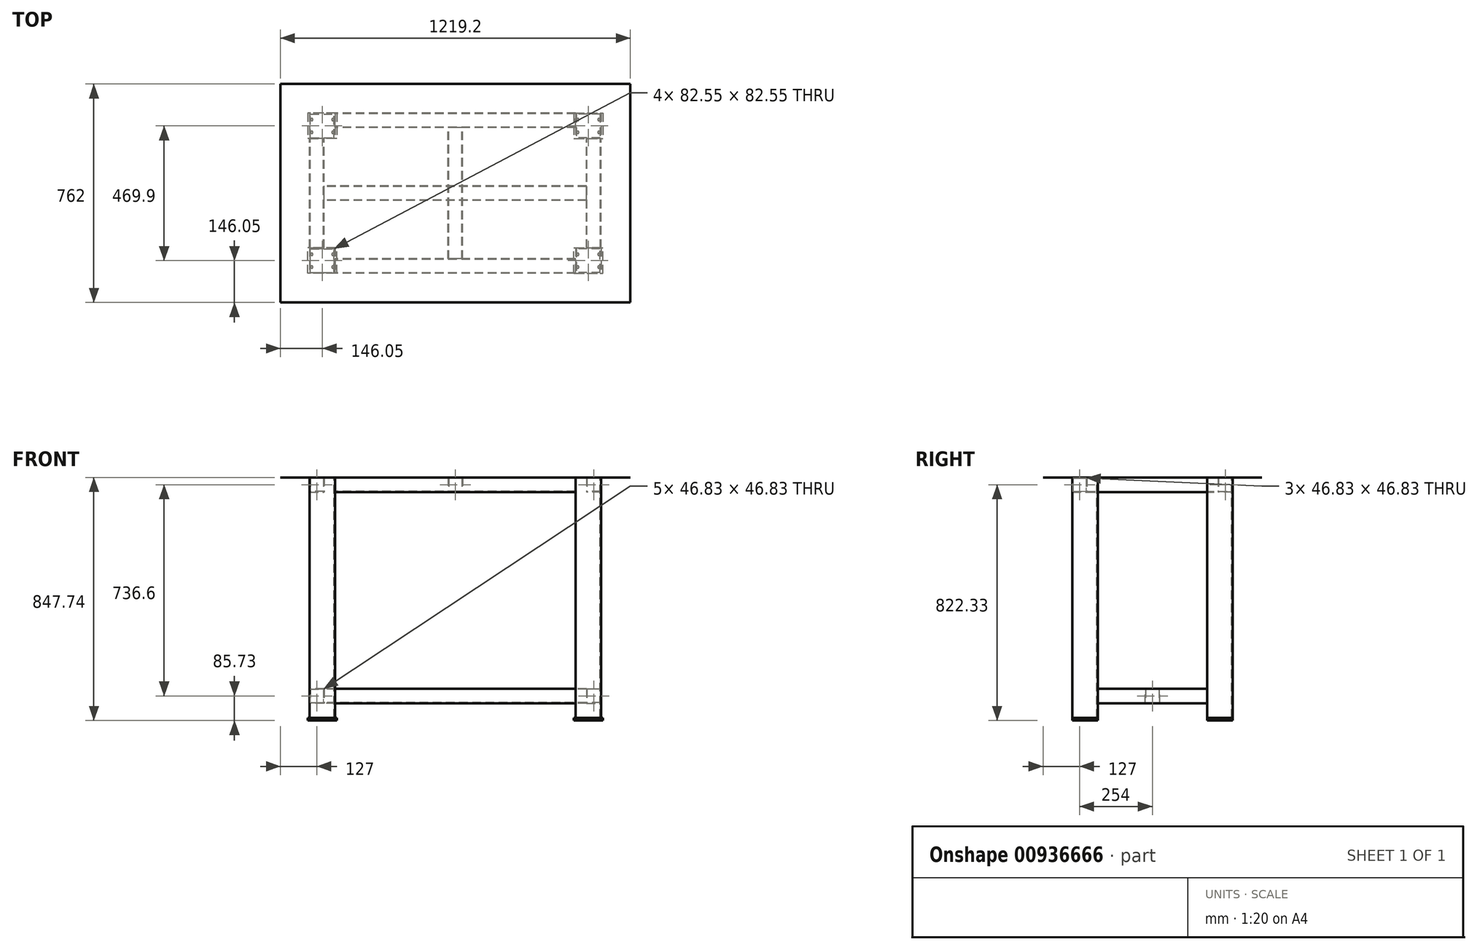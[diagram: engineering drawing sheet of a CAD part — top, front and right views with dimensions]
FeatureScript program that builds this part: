
annotation { "Feature Type Name" : "Feature", "Feature Type Description" : "" }
export const myFeature = defineFeature(function(context is Context, id is Id, definition is map)
    precondition{}
    {
        {
            var Q0;
            Q0=qCreatedBy(makeId("Top.planeOp"),FACE);
            var sketch = newSketch(context, id + "F0", { "sketchPlane" : qUnion([Q0])});
            skLineSegment(sketch, "E0.bottom", {"start": v(-419.1, 279.4) * mm, "end": v(-508, 279.4) * mm});
            skLineSegment(sketch, "E0.top", {"start": v(-419.1, 190.5) * mm, "end": v(-508, 190.5) * mm});
            skLineSegment(sketch, "E0.left", {"start": v(-419.1, 279.4) * mm, "end": v(-419.1, 190.5) * mm});
            skLineSegment(sketch, "E0.right", {"start": v(-508, 279.4) * mm, "end": v(-508, 190.5) * mm});
            skPoint(sketch, "E0.middle", {"position": v(-463.55, 234.95) * mm});
            skLineSegment(sketch, "E1.bottom", {"start": v(-419.1, -190.5) * mm, "end": v(-508, -190.5) * mm});
            skLineSegment(sketch, "E1.top", {"start": v(-419.1, -279.4) * mm, "end": v(-508, -279.4) * mm});
            skLineSegment(sketch, "E1.left", {"start": v(-419.1, -190.5) * mm, "end": v(-419.1, -279.4) * mm});
            skLineSegment(sketch, "E1.right", {"start": v(-508, -190.5) * mm, "end": v(-508, -279.4) * mm});
            skPoint(sketch, "E1.middle", {"position": v(-463.55, -234.95) * mm});
            skPoint(sketch, "E2.MirrorP", {"position": v(463.55, -234.95) * mm});
            skLineSegment(sketch, "E3.MirrorCS", {"start": v(419.1, 190.5) * mm, "end": v(508, 190.5) * mm});
            skLineSegment(sketch, "E4.MirrorCS", {"start": v(419.1, -190.5) * mm, "end": v(419.1, -279.4) * mm});
            skLineSegment(sketch, "E5.MirrorCS", {"start": v(419.1, 279.4) * mm, "end": v(419.1, 190.5) * mm});
            skLineSegment(sketch, "E6.MirrorCS", {"start": v(419.1, 279.4) * mm, "end": v(508, 279.4) * mm});
            skPoint(sketch, "E7.MirrorP", {"position": v(463.55, 234.95) * mm});
            skLineSegment(sketch, "E8.MirrorCS", {"start": v(419.1, -190.5) * mm, "end": v(508, -190.5) * mm});
            skLineSegment(sketch, "E9.MirrorCS", {"start": v(508, 279.4) * mm, "end": v(508, 190.5) * mm});
            skLineSegment(sketch, "E10.MirrorCS", {"start": v(419.1, -279.4) * mm, "end": v(508, -279.4) * mm});
            skLineSegment(sketch, "E11.MirrorCS", {"start": v(508, -190.5) * mm, "end": v(508, -279.4) * mm});
            skLineSegment(sketch, "E12.bottom", {"start": v(-504.83, 193.67) * mm, "end": v(-422.28, 193.67) * mm});
            skLineSegment(sketch, "E12.top", {"start": v(-504.83, 276.23) * mm, "end": v(-422.28, 276.23) * mm});
            skLineSegment(sketch, "E12.left", {"start": v(-504.83, 193.67) * mm, "end": v(-504.83, 276.23) * mm});
            skLineSegment(sketch, "E12.right", {"start": v(-422.28, 193.67) * mm, "end": v(-422.28, 276.23) * mm});
            skLineSegment(sketch, "E13.bottom", {"start": v(-504.83, -276.23) * mm, "end": v(-422.27, -276.23) * mm});
            skLineSegment(sketch, "E13.top", {"start": v(-504.83, -193.68) * mm, "end": v(-422.27, -193.68) * mm});
            skLineSegment(sketch, "E13.left", {"start": v(-504.83, -276.23) * mm, "end": v(-504.83, -193.68) * mm});
            skLineSegment(sketch, "E13.right", {"start": v(-422.27, -276.23) * mm, "end": v(-422.27, -193.68) * mm});
            skLineSegment(sketch, "E14.MirrorCS", {"start": v(-419.1, 190.5) * mm, "end": v(-419.1, 279.4) * mm});
            skLineSegment(sketch, "E15.MirrorCS", {"start": v(-504.83, 193.68) * mm, "end": v(-422.27, 193.68) * mm});
            skLineSegment(sketch, "E16.MirrorCS", {"start": v(-504.83, 276.23) * mm, "end": v(-422.27, 276.23) * mm});
            skLineSegment(sketch, "E17.MirrorCS", {"start": v(-504.83, 276.23) * mm, "end": v(-504.83, 193.68) * mm});
            skLineSegment(sketch, "E18.MirrorCS", {"start": v(-508, 190.5) * mm, "end": v(-508, 279.4) * mm});
            skLineSegment(sketch, "E19.MirrorCS", {"start": v(-422.27, 276.23) * mm, "end": v(-422.27, 193.68) * mm});
            skLineSegment(sketch, "E20.MirrorCS", {"start": v(-419.1, -279.4) * mm, "end": v(-419.1, -190.5) * mm});
            skLineSegment(sketch, "E21.MirrorCS", {"start": v(-422.28, -193.67) * mm, "end": v(-422.28, -276.23) * mm});
            skLineSegment(sketch, "E22.MirrorCS", {"start": v(504.83, 193.67) * mm, "end": v(422.28, 193.67) * mm});
            skLineSegment(sketch, "E23.MirrorCS", {"start": v(508, 190.5) * mm, "end": v(508, 279.4) * mm});
            skLineSegment(sketch, "E24.MirrorCS", {"start": v(422.28, -193.67) * mm, "end": v(422.28, -276.23) * mm});
            skLineSegment(sketch, "E25.MirrorCS", {"start": v(419.1, -279.4) * mm, "end": v(419.1, -190.5) * mm});
            skLineSegment(sketch, "E26.MirrorCS", {"start": v(504.83, 193.68) * mm, "end": v(422.27, 193.68) * mm});
            skLineSegment(sketch, "E27.MirrorCS", {"start": v(419.1, 190.5) * mm, "end": v(419.1, 279.4) * mm});
            skLineSegment(sketch, "E28.MirrorCS", {"start": v(504.83, -193.68) * mm, "end": v(422.27, -193.68) * mm});
            skLineSegment(sketch, "E29.MirrorCS", {"start": v(504.83, 276.23) * mm, "end": v(422.27, 276.23) * mm});
            skLineSegment(sketch, "E30.MirrorCS", {"start": v(422.27, -276.23) * mm, "end": v(422.27, -193.68) * mm});
            skLineSegment(sketch, "E31.MirrorCS", {"start": v(422.27, 276.23) * mm, "end": v(422.27, 193.68) * mm});
            skLineSegment(sketch, "E32.MirrorCS", {"start": v(504.83, 276.23) * mm, "end": v(504.83, 193.68) * mm});
            skLineSegment(sketch, "E33.MirrorCS", {"start": v(504.83, -276.23) * mm, "end": v(422.27, -276.23) * mm});
            skLineSegment(sketch, "E34.MirrorCS", {"start": v(422.28, 193.67) * mm, "end": v(422.28, 276.23) * mm});
            skLineSegment(sketch, "E35.MirrorCS", {"start": v(504.83, 193.67) * mm, "end": v(504.83, 276.23) * mm});
            skLineSegment(sketch, "E36.MirrorCS", {"start": v(504.83, 276.23) * mm, "end": v(422.28, 276.23) * mm});
            skLineSegment(sketch, "E37.MirrorCS", {"start": v(504.83, -276.23) * mm, "end": v(504.83, -193.68) * mm});
            skSolve(sketch);
        }
        {
            var Q0;
            Q0=makeQuery(id+"F0.imprint","IMPRINT",FACE,{"disambiguationData":[TD([[makeQuery(id+"F0.imprint","IMPRINT",EDGE,{"derivedFrom":sQuery(id+"F0.wireOp",EDGE,"E28.MirrorCS")}),-1.0]])]});
            var Q1;
            Q1=makeQuery(id+"F0.imprint","IMPRINT",FACE,{"disambiguationData":[TD([[makeQuery(id+"F0.imprint","IMPRINT",EDGE,{"derivedFrom":sQuery(id+"F0.wireOp",EDGE,"E26.MirrorCS")}),1.0]])]});
            var Q2;
            Q2=makeQuery(id+"F0.imprint","IMPRINT",FACE,{"disambiguationData":[TD([[makeQuery(id+"F0.imprint","IMPRINT",EDGE,{"derivedFrom":sQuery(id+"F0.wireOp",EDGE,"E1.top")}),-1.0]])]});
            var Q3;
            Q3=makeQuery(id+"F0.imprint","IMPRINT",FACE,{"disambiguationData":[TD([[makeQuery(id+"F0.imprint","IMPRINT",EDGE,{"derivedFrom":sQuery(id+"F0.wireOp",EDGE,"E15.MirrorCS")}),-1.0]])]});
            extrude(context, id + "F1", {"entities" : qUnion([Q0, Q1, Q2, Q3]), "oppositeDirection" : true, "depth" : 838.2 * mm, "offsetDistance" : 25.4 * mm});
        }
        {
            var Q0;
            Q0=qCreatedBy(makeId("Right.planeOp"),FACE);
            var sketch = newSketch(context, id + "F2", { "sketchPlane" : qUnion([Q0])});
            skLineSegment(sketch, "E38.bottom", {"start": v(-279.4, 0) * mm, "end": v(-228.6, 0) * mm});
            skLineSegment(sketch, "E38.top", {"start": v(-279.4, -50.8) * mm, "end": v(-228.6, -50.8) * mm});
            skLineSegment(sketch, "E38.left", {"start": v(-279.4, 0) * mm, "end": v(-279.4, -50.8) * mm});
            skLineSegment(sketch, "E38.right", {"start": v(-228.6, 0) * mm, "end": v(-228.6, -50.8) * mm});
            skLineSegment(sketch, "E39.bottom", {"start": v(279.4, 0) * mm, "end": v(228.6, 0) * mm});
            skLineSegment(sketch, "E39.top", {"start": v(279.4, -50.8) * mm, "end": v(228.6, -50.8) * mm});
            skLineSegment(sketch, "E39.left", {"start": v(228.6, 0) * mm, "end": v(228.6, -50.8) * mm});
            skLineSegment(sketch, "E39.right", {"start": v(279.4, 0) * mm, "end": v(279.4, -50.8) * mm});
            skLineSegment(sketch, "E40.bottom", {"start": v(230.58, -1.98) * mm, "end": v(277.42, -1.98) * mm});
            skLineSegment(sketch, "E40.top", {"start": v(230.58, -48.82) * mm, "end": v(277.42, -48.82) * mm});
            skLineSegment(sketch, "E40.left", {"start": v(230.58, -1.98) * mm, "end": v(230.58, -48.82) * mm});
            skLineSegment(sketch, "E40.right", {"start": v(277.42, -1.98) * mm, "end": v(277.42, -48.82) * mm});
            skPoint(sketch, "E40.middle", {"position": v(254, -25.4) * mm});
            skPoint(sketch, "E40.middle.positionSnap0", {"position": v(254, -50.8) * mm});
            skPoint(sketch, "E40.centerSnap0", {"position": v(254, -50.8) * mm});
            skLineSegment(sketch, "E41.bottom", {"start": v(-277.42, -1.98) * mm, "end": v(-230.58, -1.98) * mm});
            skLineSegment(sketch, "E41.top", {"start": v(-277.42, -48.82) * mm, "end": v(-230.58, -48.82) * mm});
            skLineSegment(sketch, "E41.left", {"start": v(-277.42, -1.98) * mm, "end": v(-277.42, -48.82) * mm});
            skLineSegment(sketch, "E41.right", {"start": v(-230.58, -1.98) * mm, "end": v(-230.58, -48.82) * mm});
            skPoint(sketch, "E41.middle", {"position": v(-254, -25.4) * mm});
            skPoint(sketch, "E41.middle.positionSnap0", {"position": v(-228.6, -25.4) * mm});
            skPoint(sketch, "E41.centerSnap0", {"position": v(-228.6, -25.4) * mm});
            skSolve(sketch);
        }
        {
            var Q0;
            Q0=qSketchRegion(id+"F2",true);
            extrude(context, id + "F3", {"entities" : qUnion([Q0]), "depth" : 419.1 * mm, "offsetDistance" : 25.4 * mm, "hasSecondDirection" : true, "secondDirectionOppositeDirection" : true, "secondDirectionDepth" : 419.1 * mm});
        }
        {
            var Q0;
            Q0=qCreatedBy(makeId("Front.planeOp"),FACE);
            var sketch = newSketch(context, id + "F4", { "sketchPlane" : qUnion([Q0])});
            skLineSegment(sketch, "E42.bottom", {"start": v(-508, 0) * mm, "end": v(-457.2, 0) * mm});
            skLineSegment(sketch, "E42.top", {"start": v(-508, -50.8) * mm, "end": v(-457.2, -50.8) * mm});
            skLineSegment(sketch, "E42.left", {"start": v(-508, 0) * mm, "end": v(-508, -50.8) * mm});
            skLineSegment(sketch, "E42.right", {"start": v(-457.2, 0) * mm, "end": v(-457.2, -50.8) * mm});
            skLineSegment(sketch, "E43.bottom", {"start": v(508, 0) * mm, "end": v(457.2, 0) * mm});
            skLineSegment(sketch, "E43.top", {"start": v(508, -50.8) * mm, "end": v(457.2, -50.8) * mm});
            skLineSegment(sketch, "E43.left", {"start": v(508, 0) * mm, "end": v(508, -50.8) * mm});
            skLineSegment(sketch, "E43.right", {"start": v(457.2, 0) * mm, "end": v(457.2, -50.8) * mm});
            skLineSegment(sketch, "E44.bottom", {"start": v(-457.2, -736.6) * mm, "end": v(-508, -736.6) * mm});
            skLineSegment(sketch, "E44.top", {"start": v(-457.2, -787.4) * mm, "end": v(-508, -787.4) * mm});
            skLineSegment(sketch, "E44.left", {"start": v(-457.2, -736.6) * mm, "end": v(-457.2, -787.4) * mm});
            skLineSegment(sketch, "E44.right", {"start": v(-508, -736.6) * mm, "end": v(-508, -787.4) * mm});
            skLineSegment(sketch, "E45.bottom", {"start": v(457.2, -736.6) * mm, "end": v(508, -736.6) * mm});
            skLineSegment(sketch, "E45.top", {"start": v(457.2, -787.4) * mm, "end": v(508, -787.4) * mm});
            skLineSegment(sketch, "E45.left", {"start": v(457.2, -736.6) * mm, "end": v(457.2, -787.4) * mm});
            skLineSegment(sketch, "E45.right", {"start": v(508, -736.6) * mm, "end": v(508, -787.4) * mm});
            skLineSegment(sketch, "E46.bottom", {"start": v(-459.18, -1.98) * mm, "end": v(-506.02, -1.98) * mm});
            skLineSegment(sketch, "E46.top", {"start": v(-459.18, -48.82) * mm, "end": v(-506.02, -48.82) * mm});
            skLineSegment(sketch, "E46.left", {"start": v(-459.18, -1.98) * mm, "end": v(-459.18, -48.82) * mm});
            skLineSegment(sketch, "E46.right", {"start": v(-506.02, -1.98) * mm, "end": v(-506.02, -48.82) * mm});
            skPoint(sketch, "E46.middle", {"position": v(-482.6, -25.4) * mm});
            skPoint(sketch, "E46.middle.positionSnap0", {"position": v(-508, -25.4) * mm});
            skPoint(sketch, "E46.centerSnap0", {"position": v(-508, -25.4) * mm});
            skLineSegment(sketch, "E47.bottom", {"start": v(-506.02, -738.58) * mm, "end": v(-459.18, -738.58) * mm});
            skLineSegment(sketch, "E47.top", {"start": v(-506.02, -785.42) * mm, "end": v(-459.18, -785.42) * mm});
            skLineSegment(sketch, "E47.left", {"start": v(-506.02, -738.58) * mm, "end": v(-506.02, -785.42) * mm});
            skLineSegment(sketch, "E47.right", {"start": v(-459.18, -738.58) * mm, "end": v(-459.18, -785.42) * mm});
            skPoint(sketch, "E47.middle", {"position": v(-482.6, -762) * mm});
            skPoint(sketch, "E47.middle.positionSnap0", {"position": v(-457.2, -762) * mm});
            skPoint(sketch, "E47.centerSnap0", {"position": v(-457.2, -762) * mm});
            skLineSegment(sketch, "E48.bottom", {"start": v(506.02, -738.58) * mm, "end": v(459.18, -738.58) * mm});
            skLineSegment(sketch, "E48.top", {"start": v(506.02, -785.42) * mm, "end": v(459.18, -785.42) * mm});
            skLineSegment(sketch, "E48.left", {"start": v(506.02, -738.58) * mm, "end": v(506.02, -785.42) * mm});
            skLineSegment(sketch, "E48.right", {"start": v(459.18, -738.58) * mm, "end": v(459.18, -785.42) * mm});
            skPoint(sketch, "E48.middle", {"position": v(482.6, -762) * mm});
            skPoint(sketch, "E48.middle.positionSnap0", {"position": v(457.2, -762) * mm});
            skPoint(sketch, "E48.centerSnap0", {"position": v(457.2, -762) * mm});
            skLineSegment(sketch, "E49.bottom", {"start": v(506.02, -1.98) * mm, "end": v(459.18, -1.98) * mm});
            skLineSegment(sketch, "E49.top", {"start": v(506.02, -48.82) * mm, "end": v(459.18, -48.82) * mm});
            skLineSegment(sketch, "E49.left", {"start": v(506.02, -1.98) * mm, "end": v(506.02, -48.82) * mm});
            skLineSegment(sketch, "E49.right", {"start": v(459.18, -1.98) * mm, "end": v(459.18, -48.82) * mm});
            skPoint(sketch, "E49.middle", {"position": v(482.6, -25.4) * mm});
            skSolve(sketch);
        }
        {
            var Q0;
            Q0=qSketchRegion(id+"F4",true);
            extrude(context, id + "F5", {"entities" : qUnion([Q0]), "depth" : 190.5 * mm, "offsetDistance" : 25.4 * mm, "hasSecondDirection" : true, "secondDirectionOppositeDirection" : true, "secondDirectionDepth" : 190.5 * mm});
        }
        {
            var Q0;
            Q0=qCreatedBy(makeId("Right.planeOp"),FACE);
            var sketch = newSketch(context, id + "F6", { "sketchPlane" : qUnion([Q0])});
            skLineSegment(sketch, "E50.bottom", {"start": v(-25.4, -787.4) * mm, "end": v(25.4, -787.4) * mm});
            skLineSegment(sketch, "E50.top", {"start": v(-25.4, -736.6) * mm, "end": v(25.4, -736.6) * mm});
            skLineSegment(sketch, "E50.left", {"start": v(-25.4, -787.4) * mm, "end": v(-25.4, -736.6) * mm});
            skLineSegment(sketch, "E50.right", {"start": v(25.4, -787.4) * mm, "end": v(25.4, -736.6) * mm});
            skLineSegment(sketch, "E51.bottom", {"start": v(-23.42, -738.58) * mm, "end": v(23.42, -738.58) * mm});
            skLineSegment(sketch, "E51.top", {"start": v(-23.42, -785.42) * mm, "end": v(23.42, -785.42) * mm});
            skLineSegment(sketch, "E51.left", {"start": v(-23.42, -738.58) * mm, "end": v(-23.42, -785.42) * mm});
            skLineSegment(sketch, "E51.right", {"start": v(23.42, -738.58) * mm, "end": v(23.42, -785.42) * mm});
            skPoint(sketch, "E51.middle", {"position": v(0, -762) * mm});
            skPoint(sketch, "E51.middle.positionSnap0", {"position": v(-25.4, -762) * mm});
            skPoint(sketch, "E51.centerSnap0", {"position": v(-25.4, -762) * mm});
            skSolve(sketch);
        }
        {
            var Q0;
            Q0=makeQuery(id+"F6.imprint","IMPRINT",FACE,{"disambiguationData":[TD([[makeQuery(id+"F6.imprint","IMPRINT",EDGE,{"derivedFrom":sQuery(id+"F6.wireOp",EDGE,"E50.bottom")}),1.0]])]});
            extrude(context, id + "F7", {"entities" : qUnion([Q0]), "depth" : 457.2 * mm, "offsetDistance" : 25.4 * mm, "hasSecondDirection" : true, "secondDirectionOppositeDirection" : true, "secondDirectionDepth" : 457.2 * mm});
        }
        {
            var Q0;
            Q0=qCreatedBy(makeId("Top.planeOp"),FACE);
            var sketch = newSketch(context, id + "F8", { "sketchPlane" : qUnion([Q0])});
            skLineSegment(sketch, "E52.bottom", {"start": v(609.6, -381) * mm, "end": v(-609.6, -381) * mm});
            skLineSegment(sketch, "E52.top", {"start": v(609.6, 381) * mm, "end": v(-609.6, 381) * mm});
            skLineSegment(sketch, "E52.left", {"start": v(609.6, -381) * mm, "end": v(609.6, 381) * mm});
            skLineSegment(sketch, "E52.right", {"start": v(-609.6, -381) * mm, "end": v(-609.6, 381) * mm});
            skPoint(sketch, "E52.middle", {"position": v(0, 0) * mm});
            skSolve(sketch);
        }
        {
            var Q0;
            Q0=qSketchRegion(id+"F8",true);
            extrude(context, id + "F9", {"entities" : qUnion([Q0]), "depth" : 3 / 203.2 * mm, "offsetDistance" : 25.4 * mm});
        }
        {
            var Q0;
            Q0=makeQuery(id+"F1.opExtrude","CAP_FACE",FACE,{"disambiguationData":[OSD([sQuery(id+"F0.wireOp",EDGE,"E1.top"),sQuery(id+"F0.wireOp",EDGE,"E1.right"),sQuery(id+"F0.wireOp",EDGE,"E1.bottom"),sQuery(id+"F0.wireOp",EDGE,"E13.bottom"),sQuery(id+"F0.wireOp",EDGE,"E13.top"),sQuery(id+"F0.wireOp",EDGE,"E13.left"),sQuery(id+"F0.wireOp",EDGE,"E20.MirrorCS"),sQuery(id+"F0.wireOp",EDGE,"E21.MirrorCS")])],"isStart":false});
            cPlane(context, id + "F10", {"entities" : qUnion([Q0]), "cplaneType" : CPlaneType.OFFSET, "offset" : 0 * mm, "width" : 152.4 * mm, "height" : 152.4 * mm});
        }
        {
            var Q0;
            Q0=qCreatedBy(id+"F10.planeOp",FACE);
            var sketch = newSketch(context, id + "F11", { "sketchPlane" : qUnion([Q0])});
            skLineSegment(sketch, "E53.bottom", {"start": v(-412.75, 279.4) * mm, "end": v(-514.35, 279.4) * mm});
            skLineSegment(sketch, "E53.top", {"start": v(-412.75, 190.5) * mm, "end": v(-514.35, 190.5) * mm});
            skLineSegment(sketch, "E53.left", {"start": v(-412.75, 279.4) * mm, "end": v(-412.75, 190.5) * mm});
            skLineSegment(sketch, "E53.right", {"start": v(-514.35, 279.4) * mm, "end": v(-514.35, 190.5) * mm});
            skPoint(sketch, "E53.middle", {"position": v(-463.55, 234.95) * mm});
            skSolve(sketch);
        }
        {
            var Q0;
            Q0=qSketchRegion(id+"F11",true);
            extrude(context, id + "F12", {"entities" : qUnion([Q0]), "depth" : 9.52 * mm, "offsetDistance" : 25.4 * mm});
        }
        {
            var Q0;
            Q0=makeQuery(id+"F12.opExtrude","CAP_FACE",FACE,{"disambiguationData":[OSD([sQuery(id+"F11.wireOp",EDGE,"E53.bottom"),sQuery(id+"F11.wireOp",EDGE,"E53.top"),sQuery(id+"F11.wireOp",EDGE,"E53.left"),sQuery(id+"F11.wireOp",EDGE,"E53.right")])],"isStart":false});
            cPlane(context, id + "F13", {"entities" : qUnion([Q0]), "cplaneType" : CPlaneType.OFFSET, "offset" : 0 * mm, "width" : 152.4 * mm, "height" : 152.4 * mm});
        }
        {
            var Q0;
            Q0=qCreatedBy(id+"F13.planeOp",FACE);
            var sketch = newSketch(context, id + "F14", { "sketchPlane" : qUnion([Q0])});
            skCircle(sketch, "E54", {"center": v(-427.04, 257.18) * mm, "radius": 4.76 * mm});
            skCircle(sketch, "E55", {"center": v(-427.04, 212.73) * mm, "radius": 4.76 * mm});
            skCircle(sketch, "E56", {"center": v(-500.06, 212.73) * mm, "radius": 4.76 * mm});
            skCircle(sketch, "E57", {"center": v(-500.06, 257.18) * mm, "radius": 4.76 * mm});
            skSolve(sketch);
        }
        {
            var Q0;
            Q0=sQuery(id+"F14.wireOp",VERTEX,"E57.center");
            var Q1;
            Q1=sQuery(id+"F14.wireOp",VERTEX,"E56.center");
            var Q2;
            Q2=sQuery(id+"F14.wireOp",VERTEX,"E55.center");
            var Q3;
            Q3=sQuery(id+"F14.wireOp",VERTEX,"E54.center");
            var Q4;
            Q4=makeQuery(id+"F1.opExtrude","SWEPT_BODY",BODY,{"disambiguationData":[OSD([sQuery(id+"F0.wireOp",EDGE,"E1.top"),sQuery(id+"F0.wireOp",EDGE,"E1.right"),sQuery(id+"F0.wireOp",EDGE,"E1.bottom"),sQuery(id+"F0.wireOp",EDGE,"E13.bottom"),sQuery(id+"F0.wireOp",EDGE,"E13.top"),sQuery(id+"F0.wireOp",EDGE,"E13.left"),sQuery(id+"F0.wireOp",EDGE,"E20.MirrorCS"),sQuery(id+"F0.wireOp",EDGE,"E21.MirrorCS")])]});
            var Q5;
            Q5=makeQuery(id+"F9.opExtrude","SWEPT_BODY",BODY,{"disambiguationData":[OSD([sQuery(id+"F8.wireOp",EDGE,"E52.bottom"),sQuery(id+"F8.wireOp",EDGE,"E52.top"),sQuery(id+"F8.wireOp",EDGE,"E52.left"),sQuery(id+"F8.wireOp",EDGE,"E52.right")])]});
            var Q6;
            Q6=makeQuery(id+"F12.opExtrude","SWEPT_BODY",BODY,{"disambiguationData":[OSD([sQuery(id+"F11.wireOp",EDGE,"E53.bottom"),sQuery(id+"F11.wireOp",EDGE,"E53.top"),sQuery(id+"F11.wireOp",EDGE,"E53.left"),sQuery(id+"F11.wireOp",EDGE,"E53.right")])]});
            hole(context, id + "F15", {"style" : HoleStyle.SIMPLE, "endStyle" : HoleEndStyle.BLIND, "standardTappedOrClearance" : lookupTablePath({ "standard" : "ANSI", "engagement" : "75%", "pitch" : "16 tpi", "size" : "3/8", "type" : "Tapped" }), "standardBlindInLast" : lookupTablePath({ "standard" : "ANSI", "engagement" : "75%", "pitch" : "16 tpi", "size" : "3/8", "type" : "Tapped" }), "holeDiameter" : 7.94 * mm, "majorDiameter" : 9.52 * mm, "showTappedDepth" : true, "holeDepth" : 9.52 * mm, "isTappedThrough" : true, "tappedDepth" : 4.76 * mm, "tapClearance" : 3, "locations" : qUnion([Q0, Q1, Q2, Q3]), "scope" : qUnion([Q4, Q5, Q6])});
        }
        {
            var Q0;
            Q0=makeQuery(id+"F12.opExtrude","SWEPT_BODY",BODY,{"disambiguationData":[OSD([sQuery(id+"F11.wireOp",EDGE,"E53.bottom"),sQuery(id+"F11.wireOp",EDGE,"E53.top"),sQuery(id+"F11.wireOp",EDGE,"E53.left"),sQuery(id+"F11.wireOp",EDGE,"E53.right")])]});
            var Q1;
            Q1=qCreatedBy(makeId("Front.planeOp"),FACE);
            mirror(context, id + "F16", {"entities" : qUnion([Q0]), "mirrorPlane" : qUnion([Q1])});
        }
        {
            var Q0;
            Q0=makeQuery(id+"F12.opExtrude","SWEPT_BODY",BODY,{"disambiguationData":[OSD([sQuery(id+"F11.wireOp",EDGE,"E53.bottom"),sQuery(id+"F11.wireOp",EDGE,"E53.top"),sQuery(id+"F11.wireOp",EDGE,"E53.left"),sQuery(id+"F11.wireOp",EDGE,"E53.right")])]});
            var Q1;
            Q1=makeQuery(id+"F16.opPattern","COPY",BODY,{"derivedFrom":makeQuery(id+"F12.opExtrude","SWEPT_BODY",BODY,{"disambiguationData":[OSD([sQuery(id+"F11.wireOp",EDGE,"E53.bottom"),sQuery(id+"F11.wireOp",EDGE,"E53.top"),sQuery(id+"F11.wireOp",EDGE,"E53.left"),sQuery(id+"F11.wireOp",EDGE,"E53.right")])]}),"instanceName":"1"});
            var Q2;
            Q2=qCreatedBy(makeId("Right.planeOp"),FACE);
            mirror(context, id + "F17", {"entities" : qUnion([Q0, Q1]), "mirrorPlane" : qUnion([Q2])});
        }
        {
            var Q0;
            Q0=qCreatedBy(makeId("Front.planeOp"),FACE);
            var sketch = newSketch(context, id + "F18", { "sketchPlane" : qUnion([Q0])});
            skLineSegment(sketch, "E58.bottom", {"start": v(25.4, 0) * mm, "end": v(-25.4, 0) * mm});
            skLineSegment(sketch, "E58.top", {"start": v(25.4, -50.8) * mm, "end": v(-25.4, -50.8) * mm});
            skLineSegment(sketch, "E58.left", {"start": v(25.4, 0) * mm, "end": v(25.4, -50.8) * mm});
            skLineSegment(sketch, "E58.right", {"start": v(-25.4, 0) * mm, "end": v(-25.4, -50.8) * mm});
            skPoint(sketch, "E58.middle", {"position": v(0, -25.4) * mm});
            skLineSegment(sketch, "E59.bottom", {"start": v(23.42, -1.98) * mm, "end": v(-23.42, -1.98) * mm});
            skLineSegment(sketch, "E59.top", {"start": v(23.42, -48.82) * mm, "end": v(-23.42, -48.82) * mm});
            skLineSegment(sketch, "E59.left", {"start": v(23.42, -1.98) * mm, "end": v(23.42, -48.82) * mm});
            skLineSegment(sketch, "E59.right", {"start": v(-23.42, -1.98) * mm, "end": v(-23.42, -48.82) * mm});
            skSolve(sketch);
        }
        {
            var Q0;
            Q0=makeQuery(id+"F18.imprint","IMPRINT",FACE,{"disambiguationData":[TD([[makeQuery(id+"F18.imprint","IMPRINT",EDGE,{"derivedFrom":sQuery(id+"F18.wireOp",EDGE,"E58.bottom")}),1.0]])]});
            extrude(context, id + "F19", {"entities" : qUnion([Q0]), "depth" : 228.6 * mm, "offsetDistance" : 25.4 * mm, "hasSecondDirection" : true, "secondDirectionOppositeDirection" : true, "secondDirectionDepth" : 228.6 * mm});
        }
    });
